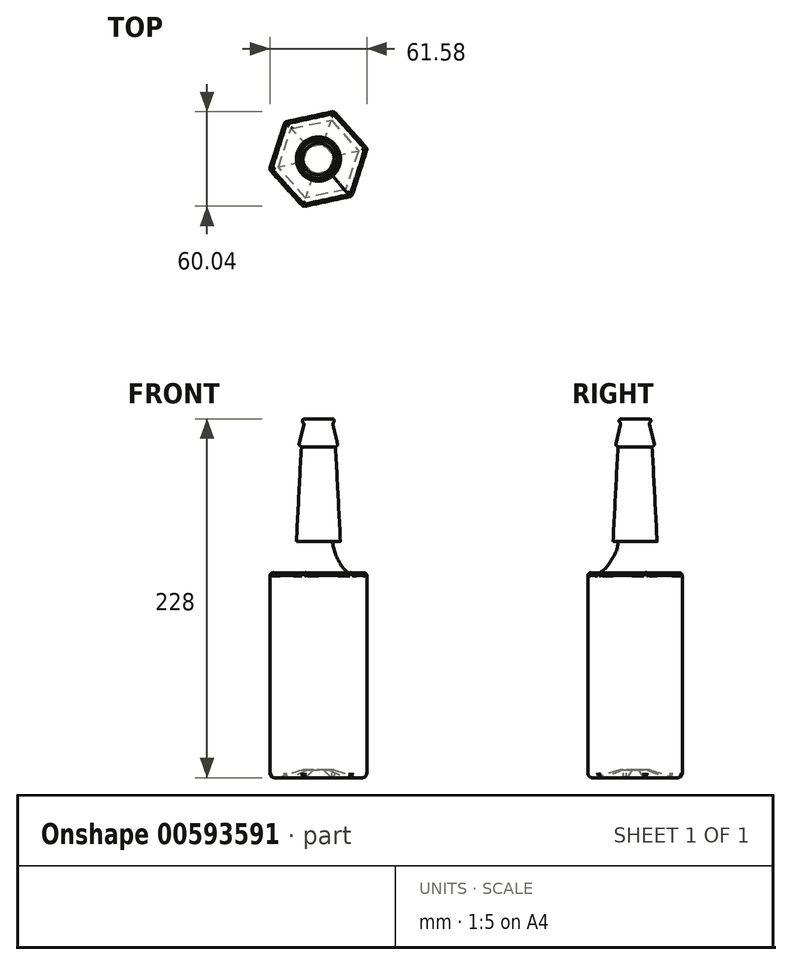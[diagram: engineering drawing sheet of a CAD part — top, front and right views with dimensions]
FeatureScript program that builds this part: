
annotation { "Feature Type Name" : "Feature", "Feature Type Description" : "" }
export const myFeature = defineFeature(function(context is Context, id is Id, definition is map)
    precondition{}
    {
        {
            var Q0;
            Q0=qCreatedBy(makeId("Top.planeOp"),FACE);
            var sketch = newSketch(context, id + "F0", { "sketchPlane" : qUnion([Q0])});
            skCircle(sketch, "E0.cCircle", {"center": v(0, 0) * mm, "radius": 27.5 * mm, "construction": true});
            skLineSegment(sketch, "E0.0", {"start": v(20.16, -23.8) * mm, "end": v(-8.63, -29.97) * mm});
            skLineSegment(sketch, "E0.1", {"start": v(-10.54, -29.36) * mm, "end": v(-30.28, -7.51) * mm});
            skLineSegment(sketch, "E0.2", {"start": v(-30.7, -5.55) * mm, "end": v(-21.64, 22.46) * mm});
            skLineSegment(sketch, "E0.3", {"start": v(-20.16, 23.8) * mm, "end": v(8.63, 29.97) * mm});
            skLineSegment(sketch, "E0.4", {"start": v(10.54, 29.36) * mm, "end": v(30.28, 7.51) * mm});
            skLineSegment(sketch, "E0.5", {"start": v(30.7, 5.55) * mm, "end": v(21.64, -22.46) * mm});
            skPoint(sketch, "E0.0.midPoint", {"position": v(5.76, -26.89) * mm});
            skPoint(sketch, "E1.visualSharp", {"position": v(-31.05, -6.65) * mm});
            skArc(sketch, "E1.filletArc", {"start": v(-30.7, -5.55) * mm, "mid": v(-30.75, -6.59) * mm, "end": v(-30.28, -7.51) * mm});
            skPoint(sketch, "E2.visualSharp", {"position": v(-21.29, 23.56) * mm});
            skArc(sketch, "E2.filletArc", {"start": v(-20.16, 23.8) * mm, "mid": v(-21.08, 23.33) * mm, "end": v(-21.64, 22.46) * mm});
            skPoint(sketch, "E3.visualSharp", {"position": v(9.76, 30.22) * mm});
            skArc(sketch, "E3.filletArc", {"start": v(10.54, 29.36) * mm, "mid": v(9.67, 29.92) * mm, "end": v(8.63, 29.97) * mm});
            skPoint(sketch, "E4.visualSharp", {"position": v(31.05, 6.65) * mm});
            skArc(sketch, "E4.filletArc", {"start": v(30.7, 5.55) * mm, "mid": v(30.75, 6.59) * mm, "end": v(30.28, 7.51) * mm});
            skPoint(sketch, "E5.visualSharp", {"position": v(21.29, -23.56) * mm});
            skArc(sketch, "E5.filletArc", {"start": v(20.16, -23.8) * mm, "mid": v(21.08, -23.33) * mm, "end": v(21.64, -22.46) * mm});
            skPoint(sketch, "E6.visualSharp", {"position": v(-9.76, -30.22) * mm});
            skArc(sketch, "E6.filletArc", {"start": v(-10.54, -29.36) * mm, "mid": v(-9.67, -29.92) * mm, "end": v(-8.63, -29.97) * mm});
            skSolve(sketch);
        }
        {
            var Q0;
            Q0=makeQuery(id+"F0.imprint","IMPRINT",FACE,{"disambiguationData":[TD([[makeQuery(id+"F0.imprint","IMPRINT",EDGE,{"derivedFrom":sQuery(id+"F0.wireOp",EDGE,"E0.0")}),-1.0]])]});
            extrude(context, id + "F1", {"entities" : qUnion([Q0]), "depth" : 130 * mm, "offsetDistance" : 25 * mm});
        }
        {
            var Q0;
            Q0=qCreatedBy(makeId("Top.planeOp"),FACE);
            cPlane(context, id + "F2", {"entities" : qUnion([Q0]), "cplaneType" : CPlaneType.OFFSET, "offset" : 150 * mm, "width" : 150 * mm, "height" : 150 * mm});
        }
        {
            var Q0;
            Q0=qCreatedBy(id+"F2.planeOp",FACE);
            var sketch = newSketch(context, id + "F3", { "sketchPlane" : qUnion([Q0])});
            skCircle(sketch, "E7", {"center": v(0, 0) * mm, "radius": 14 * mm});
            skSolve(sketch);
        }
        {
            var Q1;
            Q1=makeQuery(id+"F1.opExtrude","CAP_FACE",FACE,{"disambiguationData":[OSD([sQuery(id+"F0.wireOp",EDGE,"E0.0"),sQuery(id+"F0.wireOp",EDGE,"E0.1"),sQuery(id+"F0.wireOp",EDGE,"E0.2"),sQuery(id+"F0.wireOp",EDGE,"E0.3"),sQuery(id+"F0.wireOp",EDGE,"E0.4"),sQuery(id+"F0.wireOp",EDGE,"E0.5")])],"isStart":false});
            var Q2;
            Q2=makeQuery(id+"F3.imprint","IMPRINT",FACE,{"disambiguationData":[TD([[makeQuery(id+"F3.imprint","IMPRINT",EDGE,{"derivedFrom":sQuery(id+"F3.wireOp",EDGE,"E7")}),1.0]])]});
            loft(context, id + "F4", {"operationType" : NewBodyOperationType.ADD, "startCondition" : LoftEndDerivativeType.TANGENT_TO_PROFILE, "startMagnitude" : 1.1, "endCondition" : LoftEndDerivativeType.NORMAL_TO_PROFILE, "endMagnitude" : 1, "sheetProfilesArray" : [{ "sheetProfileEntities" : qUnion([Q1]) }, { "sheetProfileEntities" : qUnion([Q2]) }]});
        }
        {
            var Q0;
            Q0=makeQuery(id+"F4.opLoft","CAP_FACE",FACE,{"disambiguationData":[OSD([makeQuery(id+"F3.imprint","IMPRINT",FACE,{"disambiguationData":[TD([[makeQuery(id+"F3.imprint","IMPRINT",EDGE,{"derivedFrom":sQuery(id+"F3.wireOp",EDGE,"E7")}),1.0]])]})])],"isStart":true});
            extrude(context, id + "F5", {"entities" : qUnion([Q0]), "operationType" : NewBodyOperationType.ADD, "depth" : 60 * mm, "offsetDistance" : 25 * mm, "hasDraft" : true, "draftAngle" : 3 * degree, "draftPullDirection" : true});
        }
        {
            var Q0;
            Q0=qCreatedBy(makeId("Right.planeOp"),FACE);
            var sketch = newSketch(context, id + "F6", { "sketchPlane" : qUnion([Q0])});
            skArc(sketch, "E8", {"start": v(24.15, 0) * mm, "mid": v(12.16, 2.27) * mm, "end": v(0, 3.22) * mm});
            skLineSegment(sketch, "E9", {"start": v(0, 3.22) * mm, "end": v(0, 0) * mm});
            skLineSegment(sketch, "E10", {"start": v(0, 0) * mm, "end": v(24.15, 0) * mm});
            skSolve(sketch);
        }
        {
            var Q0;
            Q0=makeQuery(id+"F1.opExtrude","CAP_FACE",FACE,{"disambiguationData":[OSD([sQuery(id+"F0.wireOp",EDGE,"E0.0"),sQuery(id+"F0.wireOp",EDGE,"E0.1"),sQuery(id+"F0.wireOp",EDGE,"E0.2"),sQuery(id+"F0.wireOp",EDGE,"E0.3"),sQuery(id+"F0.wireOp",EDGE,"E0.4"),sQuery(id+"F0.wireOp",EDGE,"E0.5"),sQuery(id+"F0.wireOp",EDGE,"E1.filletArc"),sQuery(id+"F0.wireOp",EDGE,"E2.filletArc"),sQuery(id+"F0.wireOp",EDGE,"E3.filletArc"),sQuery(id+"F0.wireOp",EDGE,"E4.filletArc"),sQuery(id+"F0.wireOp",EDGE,"E5.filletArc"),sQuery(id+"F0.wireOp",EDGE,"E6.filletArc")])],"isStart":true});
            var sketch = newSketch(context, id + "F7", { "sketchPlane" : qUnion([Q0])});
            skCircle(sketch, "E11.cCircle", {"center": v(0, 0) * mm, "radius": 22.5 * mm, "construction": true});
            skLineSegment(sketch, "E11.0", {"start": v(17.24, 19.44) * mm, "end": v(25.45, -5.2) * mm});
            skLineSegment(sketch, "E11.1", {"start": v(25.45, -5.2) * mm, "end": v(8.22, -24.65) * mm});
            skLineSegment(sketch, "E11.2", {"start": v(8.22, -24.65) * mm, "end": v(-17.24, -19.44) * mm});
            skLineSegment(sketch, "E11.3", {"start": v(-17.24, -19.44) * mm, "end": v(-25.45, 5.2) * mm});
            skLineSegment(sketch, "E11.4", {"start": v(-25.45, 5.2) * mm, "end": v(-8.22, 24.65) * mm});
            skLineSegment(sketch, "E11.5", {"start": v(-8.22, 24.65) * mm, "end": v(17.24, 19.44) * mm});
            skPoint(sketch, "E11.0.midPoint", {"position": v(21.35, 7.12) * mm});
            skSolve(sketch);
        }
        {
            var Q0;
            Q0 = qSketchRegion(id + "F7", true);
            extrude(context, id + "F8", {"entities" : qUnion([Q0]), "operationType" : NewBodyOperationType.REMOVE, "oppositeDirection" : true, "depth" : 5 * mm, "offsetDistance" : 25 * mm, "hasDraft" : true, "draftAngle" : 70 * degree, "draftPullDirection" : true});
        }
        {
            var Q0;
            Q0=qCreatedBy(id+"F2.planeOp",FACE);
            cPlane(context, id + "F9", {"entities" : qUnion([Q0]), "cplaneType" : CPlaneType.OFFSET, "offset" : 70 * mm, "width" : 150 * mm, "height" : 150 * mm});
        }
        {
            var Q0;
            Q0=qCreatedBy(makeId("Front.planeOp"),FACE);
            var sketch = newSketch(context, id + "F10", { "sketchPlane" : qUnion([Q0])});
            skLineSegment(sketch, "E12", {"start": v(-10.75, 210) * mm, "end": v(-11.9, 210.95) * mm});
            skLineSegment(sketch, "E13", {"start": v(-12.22, 211.96) * mm, "end": v(-9.18, 224.38) * mm});
            skLineSegment(sketch, "E14", {"start": v(-9.3, 225.13) * mm, "end": v(-9.93, 226.18) * mm});
            skLineSegment(sketch, "E15", {"start": v(-10.06, 226.88) * mm, "end": v(-10, 227.18) * mm});
            skLineSegment(sketch, "E16", {"start": v(-9.02, 228) * mm, "end": v(0, 228) * mm});
            skLineSegment(sketch, "E17", {"start": v(0, 228) * mm, "end": v(0, 210) * mm});
            skLineSegment(sketch, "E18", {"start": v(0, 210) * mm, "end": v(-10.75, 210) * mm});
            skPoint(sketch, "E19.visualSharp", {"position": v(-9.86, 228) * mm});
            skArc(sketch, "E19.filletArc", {"start": v(-9.02, 228) * mm, "mid": v(-9.66, 227.77) * mm, "end": v(-10, 227.18) * mm});
            skPoint(sketch, "E20.visualSharp", {"position": v(-10.13, 226.5) * mm});
            skArc(sketch, "E20.filletArc", {"start": v(-10.06, 226.88) * mm, "mid": v(-10.06, 226.52) * mm, "end": v(-9.93, 226.18) * mm});
            skPoint(sketch, "E21.visualSharp", {"position": v(-9.08, 224.78) * mm});
            skArc(sketch, "E21.filletArc", {"start": v(-9.18, 224.38) * mm, "mid": v(-9.16, 224.77) * mm, "end": v(-9.3, 225.13) * mm});
            skPoint(sketch, "E22.visualSharp", {"position": v(-12.37, 211.35) * mm});
            skArc(sketch, "E22.filletArc", {"start": v(-12.22, 211.96) * mm, "mid": v(-12.2, 211.41) * mm, "end": v(-11.9, 210.95) * mm});
            skSolve(sketch);
        }
        {
            var Q0;
            Q0=makeQuery(id+"F10.imprint","IMPRINT",FACE,{"disambiguationData":[TD([[makeQuery(id+"F10.imprint","IMPRINT",EDGE,{"derivedFrom":sQuery(id+"F10.wireOp",EDGE,"E12")}),-1.0]])]});
            var Q1;
            Q1=sQuery(id+"F10.wireOp",EDGE,"E17");
            revolve(context, id + "F11", {"operationType" : NewBodyOperationType.ADD, "entities" : qUnion([Q0]), "axis" : qUnion([Q1]), "revolveType" : RevolveType.FULL});
        }
        {
            var Q0;
            Q0=makeQuery(id+"F1.opExtrude","CAP_EDGE",EDGE,{"disambiguationData":[OSD([sQuery(id+"F0.wireOp",EDGE,"E0.0")])],"isStart":true});
            fillet(context, id + "F12", {"entities" : qUnion([Q0]), "radius" : 3 * mm, "tangentPropagation" : true, "allowEdgeOverflow" : false});
        }
        {
            var Q0;
            {var subQ0=sQuery(id+"F0.wireOp",EDGE,"E0.5");Q0=makeQuery(id+"F4.boolean.opBoolean","MERGE",EDGE,{"derivedFrom":[makeQuery(id+"F1.opExtrude","CAP_EDGE",EDGE,{"disambiguationData":[OSD([subQ0])],"isStart":false}),makeQuery(id+"F4.opLoft","MID_CAP_EDGE",EDGE,{"disambiguationData":[OSD([subQ0,sQuery(id+"F0.wireOp",EDGE,"E4.filletArc"),sQuery(id+"F0.wireOp",EDGE,"E5.filletArc")])],"capPos":0.0})]});}
            fillet(context, id + "F13", {"entities" : qUnion([Q0]), "radius" : 2 * mm, "tangentPropagation" : true, "allowEdgeOverflow" : false});
        }
    });
